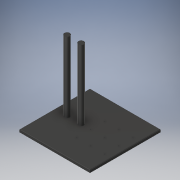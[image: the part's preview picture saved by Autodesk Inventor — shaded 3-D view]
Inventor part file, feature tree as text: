
AUTODESK INVENTOR PART (.ipt)
format: ipt  version: 2019.4 (Build 234330000, 330)  size: 128,000 bytes
history: native  units: in
note: dims shown in document units (in); Inventor stores cm internally (conversion verified against a paired STEP export)
features: extrude x2, sketch x1, hole x1, chamfer x1
ambient origin geometry x8: Origin, YZ Plane, XZ Plane, XY Plane, X Axis, Y Axis, Z Axis, Center Point
bodies: Solid1 (feature_tree)
feature tree (5):
  sketch  "Sketch1"  dims[d0=10.0in d1=10.0in d2=3.0in d3=0.875in d4=1.1811in d6=2.0in d7=1.1811in d9=2.0in d12=0.75in d13=6.25in d14=0.75in d15=2.0in d16=0.375in d17=0.0in d18=10.0in d19=0.0in d20=0.156in d21=0.38in d22=0.34in d23=1.45in d24=0.5635in d25=0.536in d26=0.8108in d27=0.0625in d28=0.125in d29=45.0deg]
  extrude  "Extrusion1"  Depth=10.0in
  extrude  "Extrusion2"  Depth=10.0in
  hole  "Hole1"  [1 undecoded]
  chamfer  "Chamfer1"  Distance=1.1811in
note: 1 required parameter value undecoded (feature->parameter linkage not recoverable at this tier; creation-order binding heuristic only, values carry confidence <= 0.55)
